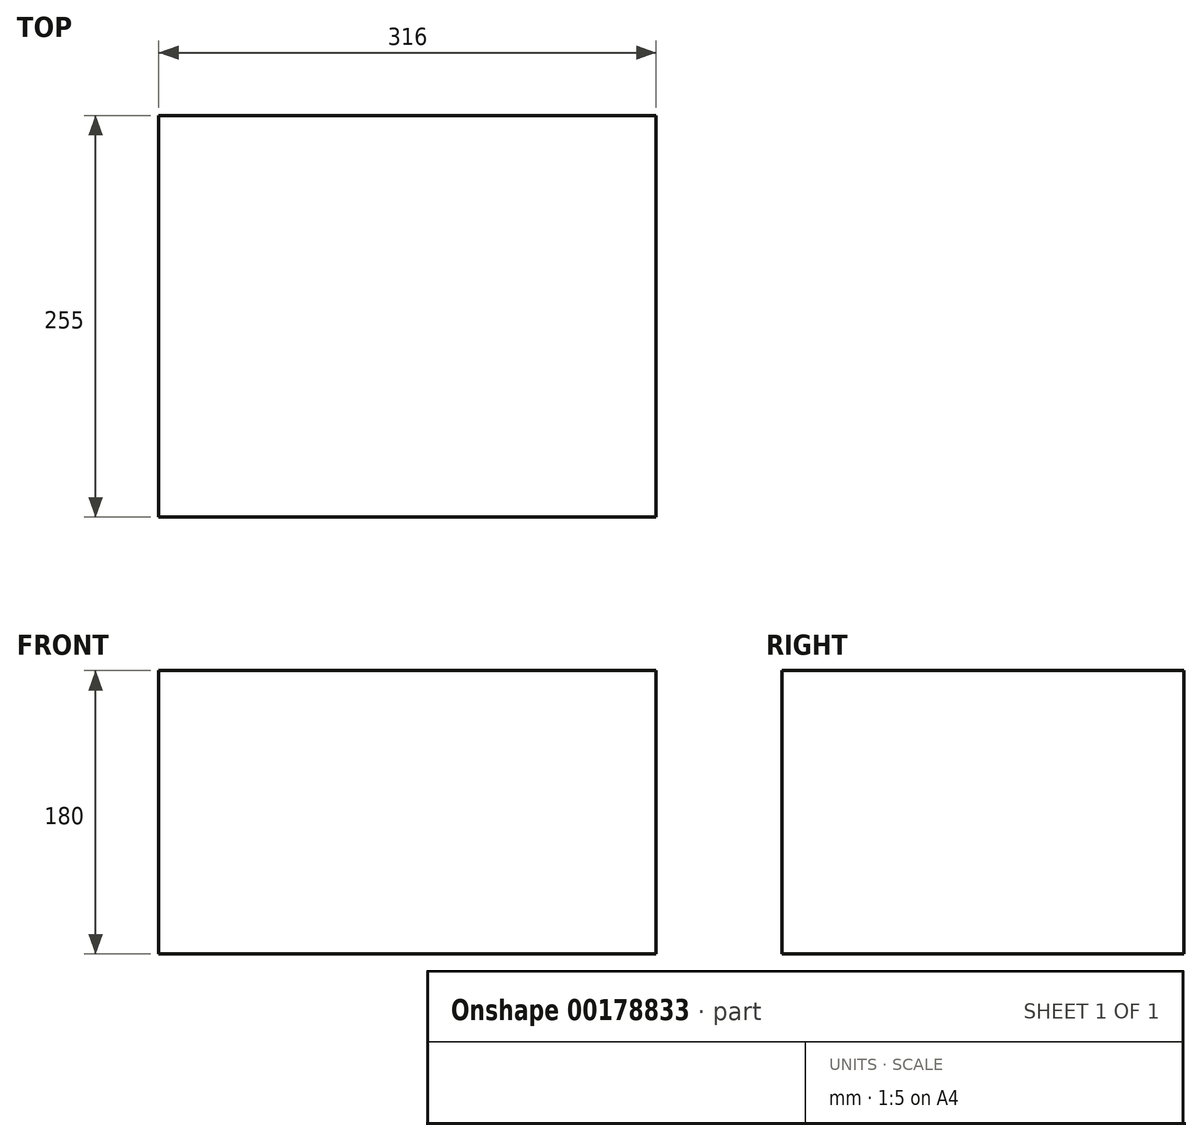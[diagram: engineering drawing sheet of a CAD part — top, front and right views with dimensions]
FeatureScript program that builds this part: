
annotation { "Feature Type Name" : "Feature", "Feature Type Description" : "" }
export const myFeature = defineFeature(function(context is Context, id is Id, definition is map)
    precondition{}
    {
        {
            var Q0;
            Q0=qCreatedBy(makeId("Front.planeOp"),FACE);
            var sketch = newSketch(context, id + "F0", { "sketchPlane" : qUnion([Q0])});
            skLineSegment(sketch, "E0.bottom", {"start": v(-232.92, 107.49) * mm, "end": v(83.08, 107.49) * mm});
            skLineSegment(sketch, "E0.top", {"start": v(-232.92, -72.51) * mm, "end": v(83.08, -72.51) * mm});
            skLineSegment(sketch, "E0.left", {"start": v(-232.92, 107.49) * mm, "end": v(-232.92, -72.51) * mm});
            skLineSegment(sketch, "E0.right", {"start": v(83.08, 107.49) * mm, "end": v(83.08, -72.51) * mm});
            skSolve(sketch);
        }
        {
            var Q0;
            Q0=makeQuery(id+"F0.imprint","IMPRINT",FACE,{"disambiguationData":[TD([[makeQuery(id+"F0.imprint","IMPRINT",EDGE,{"derivedFrom":sQuery(id+"F0.wireOp",EDGE,"E0.bottom")}),-1.0]])]});
            extrude(context, id + "F1", {"entities" : qUnion([Q0]), "oppositeDirection" : true, "depth" : 255 * mm});
        }
    });
